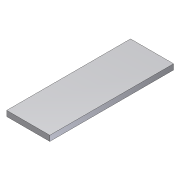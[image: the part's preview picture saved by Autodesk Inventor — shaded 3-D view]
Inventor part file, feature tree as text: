
AUTODESK INVENTOR PART (.ipt)
format: ipt  version: 2012 (Build 160160000, 160)  size: 69,120 bytes
history: native  units: in
note: dims shown in document units (in); Inventor stores cm internally (conversion verified against a paired STEP export)
features: extrude x1, sketch x1
ambient origin geometry x8: Origin, YZ Plane, XZ Plane, XY Plane, X Axis, Y Axis, Z Axis, Center Point
bodies: Solid1 (feature_tree)
feature tree (2):
  extrude  "Extrusion1"  Depth=2.0in
  sketch  "Sketch1"  dims[d5=5.75in d6=0.0in d9=2.0in d10=0.25in]
